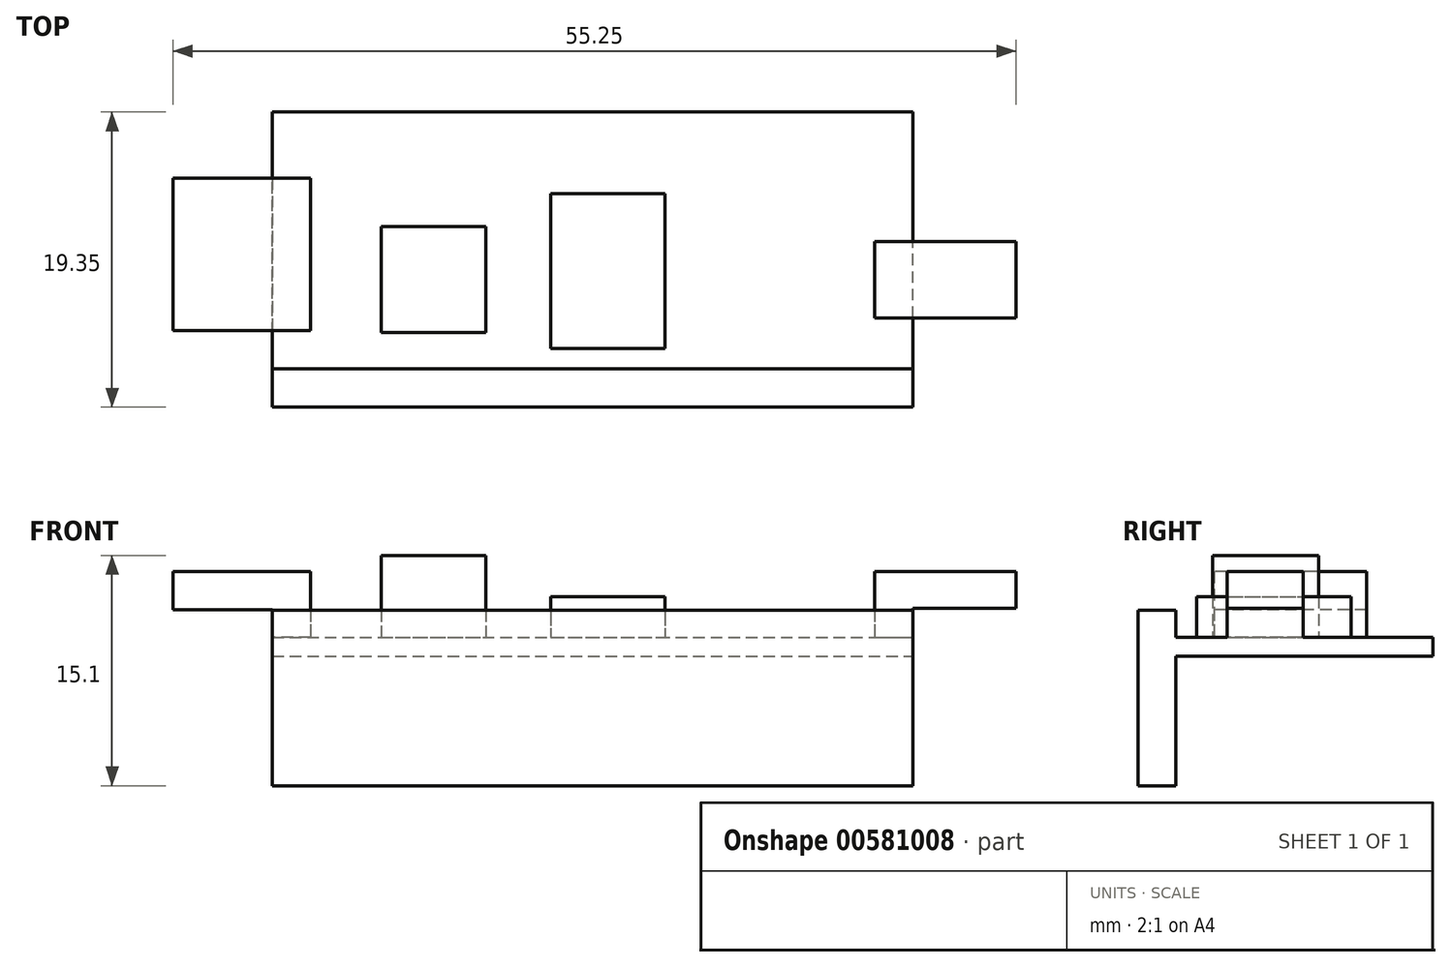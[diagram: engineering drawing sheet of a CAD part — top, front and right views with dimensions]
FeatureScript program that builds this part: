
annotation { "Feature Type Name" : "Feature", "Feature Type Description" : "" }
export const myFeature = defineFeature(function(context is Context, id is Id, definition is map)
    precondition{}
    {
        {
            var Q0;
            Q0=qCreatedBy(makeId("Top.planeOp"),FACE);
            var sketch = newSketch(context, id + "F0", { "sketchPlane" : qUnion([Q0])});
            skLineSegment(sketch, "E0.bottom", {"start": v(0, 0) * mm, "end": v(42, 0) * mm});
            skLineSegment(sketch, "E0.top", {"start": v(0, 19.35) * mm, "end": v(42, 19.35) * mm});
            skLineSegment(sketch, "E0.left", {"start": v(0, 0) * mm, "end": v(0, 19.35) * mm});
            skLineSegment(sketch, "E0.right", {"start": v(42, 0) * mm, "end": v(42, 19.35) * mm});
            skSolve(sketch);
        }
        {
            var Q0;
            Q0=makeQuery(id+"F0.imprint","IMPRINT",FACE,{"disambiguationData":[TD([[makeQuery(id+"F0.imprint","IMPRINT",EDGE,{"derivedFrom":sQuery(id+"F0.wireOp",EDGE,"E0.bottom")}),1.0]])]});
            extrude(context, id + "F1", {"entities" : qUnion([Q0]), "depth" : 1.25 * mm, "offsetDistance" : 25 * mm});
        }
        {
            var Q0;
            Q0=makeQuery(id+"F1.opExtrude","SWEPT_FACE",FACE,{"disambiguationData":[OSD([sQuery(id+"F0.wireOp",EDGE,"E0.right")])]});
            var sketch = newSketch(context, id + "F2", { "sketchPlane" : qUnion([Q0])});
            skLineSegment(sketch, "E1.bottom", {"start": v(0, 3) * mm, "end": v(2.5, 3) * mm});
            skLineSegment(sketch, "E1.top", {"start": v(0, 1.25) * mm, "end": v(2.5, 1.25) * mm});
            skLineSegment(sketch, "E1.left", {"start": v(0, 3) * mm, "end": v(0, 1.25) * mm});
            skLineSegment(sketch, "E1.right", {"start": v(2.5, 3) * mm, "end": v(2.5, 1.25) * mm});
            skLineSegment(sketch, "E2.bottom", {"start": v(0, 0) * mm, "end": v(2.5, 0) * mm});
            skLineSegment(sketch, "E2.top", {"start": v(0, -8.5) * mm, "end": v(2.5, -8.5) * mm});
            skLineSegment(sketch, "E2.left", {"start": v(0, 0) * mm, "end": v(0, -8.5) * mm});
            skLineSegment(sketch, "E2.right", {"start": v(2.5, 0) * mm, "end": v(2.5, -8.5) * mm});
            skSolve(sketch);
        }
        {
            var Q0;
            Q0=makeQuery(id+"F2.imprint","IMPRINT",FACE,{"disambiguationData":[TD([[makeQuery(id+"F2.imprint","IMPRINT",EDGE,{"derivedFrom":sQuery(id+"F2.wireOp",EDGE,"E2.bottom")}),-1.0]])]});
            var Q1;
            Q1=makeQuery(id+"F2.imprint","IMPRINT",FACE,{"disambiguationData":[TD([[makeQuery(id+"F2.imprint","IMPRINT",EDGE,{"derivedFrom":sQuery(id+"F2.wireOp",EDGE,"E1.bottom")}),-1.0]])]});
            extrude(context, id + "F3", {"entities" : qUnion([Q0, Q1]), "operationType" : NewBodyOperationType.ADD, "oppositeDirection" : true, "depth" : 42 * mm, "offsetDistance" : 25 * mm});
        }
        {
            var Q0;
            Q0=makeQuery(id+"F1.opExtrude","CAP_FACE",FACE,{"disambiguationData":[OSD([sQuery(id+"F0.wireOp",EDGE,"E0.bottom"),sQuery(id+"F0.wireOp",EDGE,"E0.top"),sQuery(id+"F0.wireOp",EDGE,"E0.left"),sQuery(id+"F0.wireOp",EDGE,"E0.right")])],"isStart":false});
            var sketch = newSketch(context, id + "F4", { "sketchPlane" : qUnion([Q0])});
            skLineSegment(sketch, "E3.bottom", {"start": v(39.5, 5.85) * mm, "end": v(48.75, 5.85) * mm});
            skLineSegment(sketch, "E3.top", {"start": v(39.5, 10.85) * mm, "end": v(48.75, 10.85) * mm});
            skLineSegment(sketch, "E3.left", {"start": v(39.5, 5.85) * mm, "end": v(39.5, 10.85) * mm});
            skLineSegment(sketch, "E3.right", {"start": v(48.75, 5.85) * mm, "end": v(48.75, 10.85) * mm});
            skLineSegment(sketch, "E4.bottom", {"start": v(2.5, 15) * mm, "end": v(-6.5, 15) * mm});
            skLineSegment(sketch, "E4.top", {"start": v(2.5, 5) * mm, "end": v(-6.5, 5) * mm});
            skLineSegment(sketch, "E4.left", {"start": v(2.5, 15) * mm, "end": v(2.5, 5) * mm});
            skLineSegment(sketch, "E4.right", {"start": v(-6.5, 15) * mm, "end": v(-6.5, 5) * mm});
            skLineSegment(sketch, "E5.bottom", {"start": v(7.15, 11.85) * mm, "end": v(14, 11.85) * mm});
            skLineSegment(sketch, "E5.top", {"start": v(7.15, 4.9) * mm, "end": v(14, 4.9) * mm});
            skLineSegment(sketch, "E5.left", {"start": v(7.15, 11.85) * mm, "end": v(7.15, 4.9) * mm});
            skLineSegment(sketch, "E5.right", {"start": v(14, 11.85) * mm, "end": v(14, 4.9) * mm});
            skLineSegment(sketch, "E6.bottom", {"start": v(18.25, 3.85) * mm, "end": v(25.75, 3.85) * mm});
            skLineSegment(sketch, "E6.top", {"start": v(18.25, 14) * mm, "end": v(25.75, 14) * mm});
            skLineSegment(sketch, "E6.left", {"start": v(18.25, 3.85) * mm, "end": v(18.25, 14) * mm});
            skLineSegment(sketch, "E6.right", {"start": v(25.75, 3.85) * mm, "end": v(25.75, 14) * mm});
            skSolve(sketch);
        }
        {
            var Q0;
            {var subQ0=sQuery(id+"F4.wireOp",EDGE,"E3.left");Q0=makeQuery(id+"F4.imprint","IMPRINT",FACE,{"disambiguationData":[TD([[makeQuery(id+"F4.imprint","IMPRINT",EDGE,{"derivedFrom":subQ0}),-1.0]])]});}
            var Q1;
            {var subQ0=sQuery(id+"F4.wireOp",EDGE,"E3.right");Q1=makeQuery(id+"F4.imprint","IMPRINT",FACE,{"disambiguationData":[TD([[makeQuery(id+"F4.imprint","IMPRINT",EDGE,{"derivedFrom":subQ0}),1.0]])]});}
            var Q2;
            {var subQ0=sQuery(id+"F4.wireOp",EDGE,"E4.right");Q2=makeQuery(id+"F4.imprint","IMPRINT",FACE,{"disambiguationData":[TD([[makeQuery(id+"F4.imprint","IMPRINT",EDGE,{"derivedFrom":subQ0}),1.0]])]});}
            var Q3;
            {var subQ0=sQuery(id+"F4.wireOp",EDGE,"E4.left");Q3=makeQuery(id+"F4.imprint","IMPRINT",FACE,{"disambiguationData":[TD([[makeQuery(id+"F4.imprint","IMPRINT",EDGE,{"derivedFrom":subQ0}),-1.0]])]});}
            extrude(context, id + "F5", {"entities" : qUnion([Q0, Q1, Q2, Q3]), "operationType" : NewBodyOperationType.ADD, "depth" : 4.3 * mm, "offsetDistance" : 25 * mm});
        }
        {
            var Q0;
            Q0=makeQuery(id+"F5.opExtrude","SWEPT_FACE",FACE,{"disambiguationData":[OSD([sQuery(id+"F4.wireOp",EDGE,"E3.right")])]});
            var sketch = newSketch(context, id + "F6", { "sketchPlane" : qUnion([Q0])});
            skLineSegment(sketch, "E7.bottom", {"start": v(5.85, 5.55) * mm, "end": v(10.85, 5.55) * mm});
            skLineSegment(sketch, "E7.top", {"start": v(5.85, 3.15) * mm, "end": v(10.85, 3.15) * mm});
            skLineSegment(sketch, "E7.left", {"start": v(5.85, 5.55) * mm, "end": v(5.85, 3.15) * mm});
            skLineSegment(sketch, "E7.right", {"start": v(10.85, 5.55) * mm, "end": v(10.85, 3.15) * mm});
            skSolve(sketch);
        }
        {
            var Q0;
            {var subQ0=sQuery(id+"F6.wireOp",EDGE,"E7.top");Q0=makeQuery(id+"F6.imprint","IMPRINT",FACE,{"disambiguationData":[TD([[makeQuery(id+"F6.imprint","IMPRINT",EDGE,{"derivedFrom":subQ0}),-1.0]])]});}
            extrude(context, id + "F7", {"entities" : qUnion([Q0]), "operationType" : NewBodyOperationType.REMOVE, "oppositeDirection" : true, "depth" : 6.75 * mm, "offsetDistance" : 25 * mm});
        }
        {
            var Q0;
            Q0=makeQuery(id+"F5.opExtrude","SWEPT_FACE",FACE,{"disambiguationData":[OSD([sQuery(id+"F4.wireOp",EDGE,"E4.right")])]});
            var sketch = newSketch(context, id + "F8", { "sketchPlane" : qUnion([Q0])});
            skLineSegment(sketch, "E8.bottom", {"start": v(-15, 5.55) * mm, "end": v(-5, 5.55) * mm});
            skLineSegment(sketch, "E8.top", {"start": v(-15, 3.05) * mm, "end": v(-5, 3.05) * mm});
            skLineSegment(sketch, "E8.left", {"start": v(-15, 5.55) * mm, "end": v(-15, 3.05) * mm});
            skLineSegment(sketch, "E8.right", {"start": v(-5, 5.55) * mm, "end": v(-5, 3.05) * mm});
            skSolve(sketch);
        }
        {
            var Q0;
            {var subQ0=sQuery(id+"F8.wireOp",EDGE,"E8.top");Q0=makeQuery(id+"F8.imprint","IMPRINT",FACE,{"disambiguationData":[TD([[makeQuery(id+"F8.imprint","IMPRINT",EDGE,{"derivedFrom":subQ0}),-1.0]])]});}
            extrude(context, id + "F9", {"entities" : qUnion([Q0]), "operationType" : NewBodyOperationType.REMOVE, "oppositeDirection" : true, "depth" : 6.5 * mm, "offsetDistance" : 25 * mm});
        }
        {
            var Q0;
            Q0=makeQuery(id+"F4.imprint","IMPRINT",FACE,{"disambiguationData":[TD([[makeQuery(id+"F4.imprint","IMPRINT",EDGE,{"derivedFrom":sQuery(id+"F4.wireOp",EDGE,"E5.bottom")}),-1.0]])]});
            extrude(context, id + "F10", {"entities" : qUnion([Q0]), "operationType" : NewBodyOperationType.ADD, "depth" : 5.35 * mm, "offsetDistance" : 25 * mm});
        }
        {
            var Q0;
            Q0=makeQuery(id+"F4.imprint","IMPRINT",FACE,{"disambiguationData":[TD([[makeQuery(id+"F4.imprint","IMPRINT",EDGE,{"derivedFrom":sQuery(id+"F4.wireOp",EDGE,"E6.bottom")}),1.0]])]});
            extrude(context, id + "F11", {"entities" : qUnion([Q0]), "operationType" : NewBodyOperationType.ADD, "depth" : 2.65 * mm, "offsetDistance" : 25 * mm});
        }
        {
            var Q0;
            Q0=makeQuery(id+"F7.boolean.opBoolean","MERGE",FACE,{"derivedFrom":[makeQuery(id+"F3.boolean.opBoolean","MERGE",FACE,{"derivedFrom":[makeQuery(id+"F1.opExtrude","SWEPT_FACE",FACE,{"disambiguationData":[OSD([sQuery(id+"F0.wireOp",EDGE,"E0.right")])]}),makeQuery(id+"F3.opExtrude","CAP_FACE",FACE,{"disambiguationData":[OSD([sQuery(id+"F2.wireOp",EDGE,"E1.bottom"),sQuery(id+"F2.wireOp",EDGE,"E1.top"),sQuery(id+"F2.wireOp",EDGE,"E1.left"),sQuery(id+"F2.wireOp",EDGE,"E1.right")])],"isStart":true}),makeQuery(id+"F3.opExtrude","CAP_FACE",FACE,{"disambiguationData":[OSD([sQuery(id+"F2.wireOp",EDGE,"E2.bottom"),sQuery(id+"F2.wireOp",EDGE,"E2.top"),sQuery(id+"F2.wireOp",EDGE,"E2.left"),sQuery(id+"F2.wireOp",EDGE,"E2.right")])],"isStart":true})]}),makeQuery(id+"F7.opExtrude","CAP_FACE",FACE,{"disambiguationData":[OSD([sQuery(id+"F4.wireOp",EDGE,"E3.bottom"),sQuery(id+"F4.wireOp",EDGE,"E3.top"),sQuery(id+"F4.wireOp",EDGE,"E3.right"),sQuery(id+"F6.wireOp",EDGE,"E7.top")])],"isStart":false})]});
            var sketch = newSketch(context, id + "F12", { "sketchPlane" : qUnion([Q0])});
            skLineSegment(sketch, "E9", {"start": v(2.5, 0) * mm, "end": v(2.5, -2.5) * mm});
            skLineSegment(sketch, "E10", {"start": v(2.5, -2.5) * mm, "end": v(0, -2.5) * mm});
            skLineSegment(sketch, "E11", {"start": v(0, -2.5) * mm, "end": v(0, 0) * mm});
            skLineSegment(sketch, "E12", {"start": v(0, 0) * mm, "end": v(2.5, 0) * mm});
            skSolve(sketch);
        }
    });
